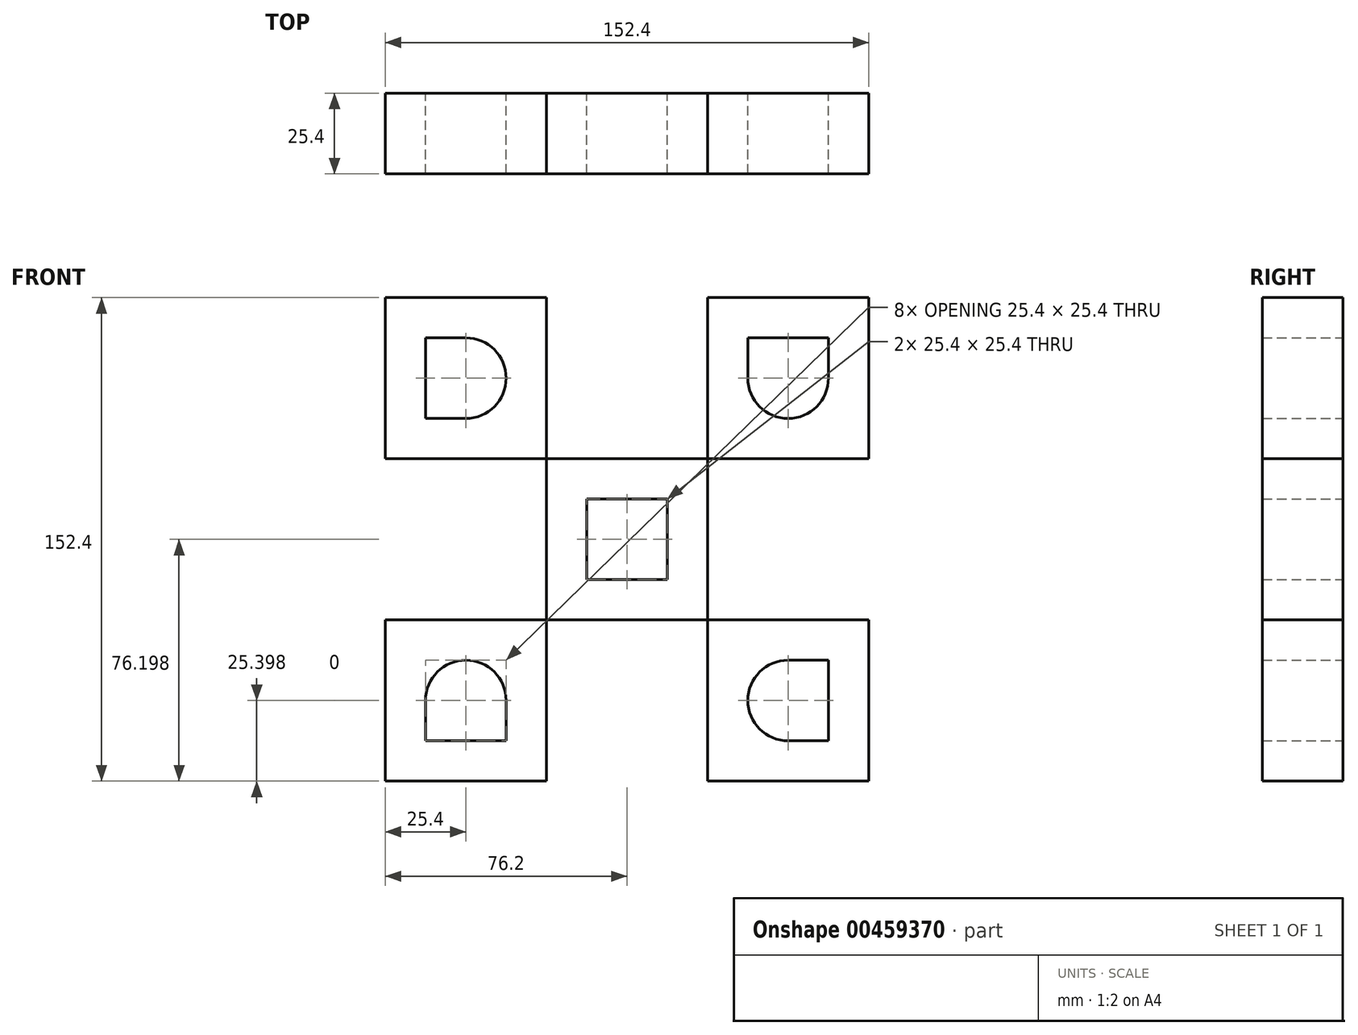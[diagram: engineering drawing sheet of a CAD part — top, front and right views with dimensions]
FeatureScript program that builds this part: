
annotation { "Feature Type Name" : "Feature", "Feature Type Description" : "" }
export const myFeature = defineFeature(function(context is Context, id is Id, definition is map)
    precondition{}
    {
        {
            var Q0;
            Q0=qCreatedBy(makeId("Front.planeOp"),FACE);
            var sketch = newSketch(context, id + "F0", { "sketchPlane" : qUnion([Q0])});
            skLineSegment(sketch, "E0.bottom", {"start": v(-12.7, 16.17) * mm, "end": v(38.1, 16.17) * mm});
            skLineSegment(sketch, "E0.top", {"start": v(-12.7, -34.63) * mm, "end": v(38.1, -34.63) * mm});
            skLineSegment(sketch, "E0.left", {"start": v(-12.7, 16.17) * mm, "end": v(-12.7, -34.63) * mm});
            skLineSegment(sketch, "E0.right", {"start": v(38.1, 16.17) * mm, "end": v(38.1, -34.63) * mm});
            skLineSegment(sketch, "E1.bottom", {"start": v(38.1, 16.17) * mm, "end": v(88.9, 16.17) * mm});
            skLineSegment(sketch, "E1.top", {"start": v(38.1, 66.97) * mm, "end": v(88.9, 66.97) * mm});
            skLineSegment(sketch, "E1.left", {"start": v(38.1, 16.17) * mm, "end": v(38.1, 66.97) * mm});
            skLineSegment(sketch, "E1.right", {"start": v(88.9, 16.17) * mm, "end": v(88.9, 66.97) * mm});
            skLineSegment(sketch, "E2.bottom", {"start": v(-12.7, -34.63) * mm, "end": v(-63.5, -34.63) * mm});
            skLineSegment(sketch, "E2.top", {"start": v(-12.7, -85.43) * mm, "end": v(-63.5, -85.43) * mm});
            skLineSegment(sketch, "E2.left", {"start": v(-12.7, -34.63) * mm, "end": v(-12.7, -85.43) * mm});
            skLineSegment(sketch, "E2.right", {"start": v(-63.5, -34.63) * mm, "end": v(-63.5, -85.43) * mm});
            skLineSegment(sketch, "E3.bottom", {"start": v(38.1, -34.63) * mm, "end": v(88.9, -34.63) * mm});
            skLineSegment(sketch, "E3.top", {"start": v(38.1, -85.43) * mm, "end": v(88.9, -85.43) * mm});
            skLineSegment(sketch, "E3.left", {"start": v(38.1, -34.63) * mm, "end": v(38.1, -85.43) * mm});
            skLineSegment(sketch, "E3.right", {"start": v(88.9, -34.63) * mm, "end": v(88.9, -85.43) * mm});
            skLineSegment(sketch, "E4.bottom", {"start": v(-12.7, 16.17) * mm, "end": v(-63.5, 16.17) * mm});
            skLineSegment(sketch, "E4.top", {"start": v(-12.7, 66.97) * mm, "end": v(-63.5, 66.97) * mm});
            skLineSegment(sketch, "E4.left", {"start": v(-12.7, 16.17) * mm, "end": v(-12.7, 66.97) * mm});
            skLineSegment(sketch, "E4.right", {"start": v(-63.5, 16.17) * mm, "end": v(-63.5, 66.97) * mm});
            skLineSegment(sketch, "E5.bottom", {"start": v(0, -21.93) * mm, "end": v(25.4, -21.93) * mm});
            skLineSegment(sketch, "E5.top", {"start": v(0, 3.47) * mm, "end": v(25.4, 3.47) * mm});
            skLineSegment(sketch, "E5.left", {"start": v(0, -21.93) * mm, "end": v(0, 3.47) * mm});
            skLineSegment(sketch, "E5.right", {"start": v(25.4, -21.93) * mm, "end": v(25.4, 3.47) * mm});
            skPoint(sketch, "E5.middle", {"position": v(12.7, -9.23) * mm});
            skPoint(sketch, "E5.middle.positionSnap0", {"position": v(38.1, -9.23) * mm});
            skPoint(sketch, "E5.middle.positionSnap1", {"position": v(12.7, 16.17) * mm});
            skPoint(sketch, "E5.centerSnap0", {"position": v(38.1, -9.23) * mm});
            skPoint(sketch, "E5.centerSnap1", {"position": v(12.7, 16.17) * mm});
            skLineSegment(sketch, "E6.bottom", {"start": v(-50.8, 54.27) * mm, "end": v(-38.1, 54.27) * mm});
            skLineSegment(sketch, "E6.top", {"start": v(-50.8, 28.87) * mm, "end": v(-38.1, 28.87) * mm});
            skLineSegment(sketch, "E6.left", {"start": v(-50.8, 54.27) * mm, "end": v(-50.8, 28.87) * mm});
            skPoint(sketch, "E6.middle", {"position": v(-38.1, 41.57) * mm});
            skPoint(sketch, "E6.middle.positionSnap0", {"position": v(-12.7, 41.57) * mm});
            skPoint(sketch, "E6.middle.positionSnap1", {"position": v(-38.1, 66.97) * mm});
            skPoint(sketch, "E6.centerSnap0", {"position": v(-12.7, 41.57) * mm});
            skPoint(sketch, "E6.centerSnap1", {"position": v(-38.1, 66.97) * mm});
            skLineSegment(sketch, "E7.top", {"start": v(76.2, 54.27) * mm, "end": v(50.8, 54.27) * mm});
            skLineSegment(sketch, "E7.left", {"start": v(76.2, 41.57) * mm, "end": v(76.2, 54.27) * mm});
            skLineSegment(sketch, "E7.right", {"start": v(50.8, 41.57) * mm, "end": v(50.8, 54.27) * mm});
            skPoint(sketch, "E7.middle", {"position": v(63.5, 41.57) * mm});
            skPoint(sketch, "E7.middle.positionSnap0", {"position": v(88.9, 41.57) * mm});
            skPoint(sketch, "E7.middle.positionSnap1", {"position": v(63.5, 66.97) * mm});
            skPoint(sketch, "E7.centerSnap0", {"position": v(88.9, 41.57) * mm});
            skPoint(sketch, "E7.centerSnap1", {"position": v(63.5, 66.97) * mm});
            skLineSegment(sketch, "E8.top", {"start": v(-50.8, -72.73) * mm, "end": v(-25.4, -72.73) * mm});
            skLineSegment(sketch, "E8.left", {"start": v(-50.8, -60.03) * mm, "end": v(-50.8, -72.73) * mm});
            skLineSegment(sketch, "E8.right", {"start": v(-25.4, -60.03) * mm, "end": v(-25.4, -72.73) * mm});
            skPoint(sketch, "E8.middle", {"position": v(-38.1, -60.03) * mm});
            skPoint(sketch, "E8.middle.positionSnap0", {"position": v(-12.7, -60.03) * mm});
            skPoint(sketch, "E8.middle.positionSnap1", {"position": v(-38.1, -34.63) * mm});
            skPoint(sketch, "E8.centerSnap0", {"position": v(-12.7, -60.03) * mm});
            skPoint(sketch, "E8.centerSnap1", {"position": v(-38.1, -34.63) * mm});
            skLineSegment(sketch, "E9.bottom", {"start": v(63.5, -47.33) * mm, "end": v(76.2, -47.33) * mm});
            skLineSegment(sketch, "E9.top", {"start": v(63.5, -72.73) * mm, "end": v(76.2, -72.73) * mm});
            skLineSegment(sketch, "E9.right", {"start": v(76.2, -47.33) * mm, "end": v(76.2, -72.73) * mm});
            skPoint(sketch, "E9.middle", {"position": v(63.5, -60.03) * mm});
            skPoint(sketch, "E9.middle.positionSnap0", {"position": v(88.9, -60.03) * mm});
            skPoint(sketch, "E9.middle.positionSnap1", {"position": v(63.5, -34.63) * mm});
            skPoint(sketch, "E9.centerSnap0", {"position": v(88.9, -60.03) * mm});
            skPoint(sketch, "E9.centerSnap1", {"position": v(63.5, -34.63) * mm});
            skArc(sketch, "E10", {"start": v(50.8, 41.57) * mm, "mid": v(63.5, 28.87) * mm, "end": v(76.2, 41.57) * mm});
            skArc(sketch, "E11", {"start": v(-38.1, 28.87) * mm, "mid": v(-25.4, 41.57) * mm, "end": v(-38.1, 54.27) * mm});
            skArc(sketch, "E12", {"start": v(63.5, -47.33) * mm, "mid": v(50.8, -60.03) * mm, "end": v(63.5, -72.73) * mm});
            skArc(sketch, "E13", {"start": v(-25.4, -60.03) * mm, "mid": v(-38.1, -47.33) * mm, "end": v(-50.8, -60.03) * mm});
            skPoint(sketch, "E14.orphan", {"position": v(-25.4, 54.27) * mm});
            skPoint(sketch, "E15.orphan", {"position": v(-25.4, 28.87) * mm});
            skPoint(sketch, "E16.orphan", {"position": v(-25.4, -47.33) * mm});
            skPoint(sketch, "E17.orphan", {"position": v(-50.8, -47.33) * mm});
            skPoint(sketch, "E18.orphan", {"position": v(50.8, 28.87) * mm});
            skPoint(sketch, "E7.bottom.start.orphan", {"position": v(76.2, 28.87) * mm});
            skPoint(sketch, "E19.orphan", {"position": v(50.8, -47.33) * mm});
            skPoint(sketch, "E9.left.end.orphan", {"position": v(50.8, -72.73) * mm});
            skSolve(sketch);
        }
        {
            var Q0;
            Q0 = qSketchRegion(id + "F0", true);
            extrude(context, id + "F1", {"entities" : qUnion([Q0]), "depth" : 25.4 * mm});
        }
        {
            var Q0;
            Q0 = qSketchRegion(id + "F0", true);
            extrude(context, id + "F2", {"entities" : qUnion([Q0]), "depth" : 25.4 * mm});
        }
    });
